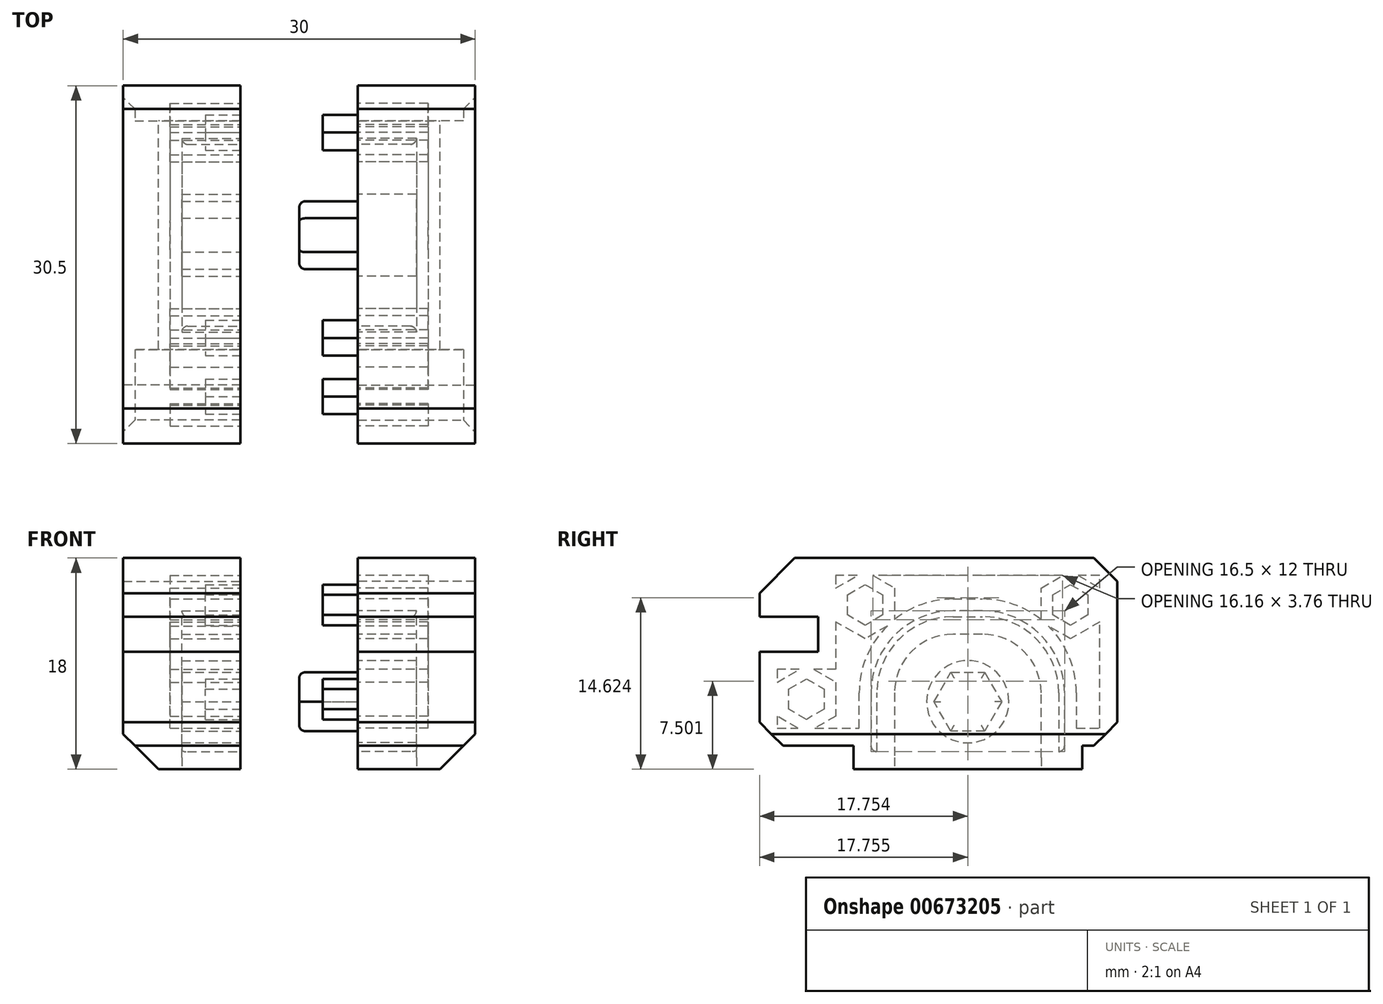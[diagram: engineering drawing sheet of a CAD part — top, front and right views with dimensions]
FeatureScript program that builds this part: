
annotation { "Feature Type Name" : "Feature", "Feature Type Description" : "" }
export const myFeature = defineFeature(function(context is Context, id is Id, definition is map)
    precondition{}
    {
        {
            var Q0;
            Q0=qCreatedBy(makeId("Right.planeOp"),FACE);
            var sketch = newSketch(context, id + "F0", { "sketchPlane" : qUnion([Q0])});
            skArc(sketch, "E0.0", {"start": v(4.44, 6.1) * mm, "mid": v(2.98, 9.63) * mm, "end": v(-0.56, 11.1) * mm});
            skLineSegment(sketch, "E0.1", {"start": v(4.44, 0.6) * mm, "end": v(4.44, 6.1) * mm});
            skLineSegment(sketch, "E0.2", {"start": v(-0.56, 11.1) * mm, "end": v(-3.06, 11.1) * mm});
            skArc(sketch, "E0.5", {"start": v(-3.06, 11.1) * mm, "mid": v(-6.6, 9.63) * mm, "end": v(-8.06, 6.1) * mm});
            skLineSegment(sketch, "E0.6", {"start": v(-8.06, 6.1) * mm, "end": v(-8.06, 0.6) * mm});
            skLineSegment(sketch, "E1", {"start": v(-1.8, 11.1) * mm, "end": v(-1.8, 5.34) * mm, "construction": true});
            skCircle(sketch, "E2", {"center": v(-1.8, 5.34) * mm, "radius": 3.5 * mm});
            skLineSegment(sketch, "E3.0", {"start": v(-10.06, 6.1) * mm, "end": v(-10.06, 1.6) * mm});
            skLineSegment(sketch, "E3.1", {"start": v(6.44, 1.6) * mm, "end": v(6.44, 6.1) * mm});
            skArc(sketch, "E3.2", {"start": v(6.44, 6.1) * mm, "mid": v(4.4, 11.04) * mm, "end": v(-0.56, 13.1) * mm});
            skLineSegment(sketch, "E3.3", {"start": v(-0.56, 13.1) * mm, "end": v(-3.06, 13.1) * mm});
            skArc(sketch, "E3.4", {"start": v(-3.06, 13.1) * mm, "mid": v(-8, 11.04) * mm, "end": v(-10.06, 6.1) * mm});
            skLineSegment(sketch, "E4", {"start": v(4.44, -0.4) * mm, "end": v(-8.06, -0.4) * mm});
            skPoint(sketch, "E5.visualSharp", {"position": v(6.44, -0.4) * mm});
            skArc(sketch, "E5.filletArc", {"start": v(4.44, -0.4) * mm, "mid": v(5.86, 0.18) * mm, "end": v(6.44, 1.6) * mm});
            skPoint(sketch, "E6.visualSharp", {"position": v(-10.06, -0.4) * mm});
            skArc(sketch, "E6.filletArc", {"start": v(-10.06, 1.6) * mm, "mid": v(-9.47, 0.18) * mm, "end": v(-8.06, -0.4) * mm});
            skLineSegment(sketch, "E7", {"start": v(-6.63, -0.4) * mm, "end": v(-6.63, 0.6) * mm, "construction": true});
            skLineSegment(sketch, "E8", {"start": v(-8.06, 0.6) * mm, "end": v(-8.06, -0.4) * mm});
            skLineSegment(sketch, "E9", {"start": v(4.44, 0.6) * mm, "end": v(4.44, -0.4) * mm});
            skSolve(sketch);
        }
        {
            var Q0;
            Q0=makeQuery(id+"F0.imprint","IMPRINT",FACE,{"disambiguationData":[TD([[makeQuery(id+"F0.imprint","IMPRINT",EDGE,{"derivedFrom":sQuery(id+"F0.wireOp",EDGE,"E0.0")}),1.0]])]});
            var Q1;
            Q1=makeQuery(id+"F0.imprint","IMPRINT",FACE,{"disambiguationData":[TD([[makeQuery(id+"F0.imprint","IMPRINT",EDGE,{"derivedFrom":sQuery(id+"F0.wireOp",EDGE,"E0.0")}),-1.0]])]});
            var Q2;
            Q2=makeQuery(id+"F0.imprint","IMPRINT",FACE,{"disambiguationData":[TD([[makeQuery(id+"F0.imprint","IMPRINT",EDGE,{"derivedFrom":sQuery(id+"F0.wireOp",EDGE,"E2")}),1.0]])]});
            extrude(context, id + "F1", {"entities" : qUnion([Q0, Q1, Q2]), "oppositeDirection" : true, "depth" : 10 * mm});
        }
        {
            var Q0;
            Q0=makeQuery(id+"F0.imprint","IMPRINT",FACE,{"disambiguationData":[TD([[makeQuery(id+"F0.imprint","IMPRINT",EDGE,{"derivedFrom":sQuery(id+"F0.wireOp",EDGE,"E0.0")}),1.0]])]});
            extrude(context, id + "F2", {"entities" : qUnion([Q0]), "operationType" : NewBodyOperationType.REMOVE, "oppositeDirection" : true, "depth" : 5 * mm});
        }
        {
            var Q0;
            {var subQ0=sQuery(id+"F0.wireOp",EDGE,"E6.filletArc");var subQ1=sQuery(id+"F0.wireOp",EDGE,"E5.filletArc");var subQ2=sQuery(id+"F0.wireOp",EDGE,"E3.4");var subQ3=sQuery(id+"F0.wireOp",EDGE,"E3.0");var subQ4=sQuery(id+"F0.wireOp",EDGE,"E3.1");var subQ5=sQuery(id+"F0.wireOp",EDGE,"E3.2");var subQ6=sQuery(id+"F0.wireOp",EDGE,"E3.3");Q0=makeQuery(id+"F2.boolean.opBoolean","SPLIT",FACE,{"disambiguationData":[TD([makeQuery(id+"F1.opExtrude","SWEPT_FACE",FACE,{"disambiguationData":[OSD([subQ3])]})])],"derivedFrom":makeQuery(id+"F1.opExtrude","CAP_FACE",FACE,{"disambiguationData":[OSD([subQ3,subQ4,subQ5,subQ6,subQ2,sQuery(id+"F0.wireOp",EDGE,"E4"),subQ1,subQ0])],"isStart":true})});}
            var sketch = newSketch(context, id + "F3", { "sketchPlane" : qUnion([Q0])});
            skArc(sketch, "E10.3", {"start": v(7.94, 6.1) * mm, "mid": v(5.45, 12.1) * mm, "end": v(-0.56, 14.6) * mm});
            skLineSegment(sketch, "E10.4", {"start": v(7.94, 1.6) * mm, "end": v(7.94, 6.1) * mm});
            skLineSegment(sketch, "E10.7", {"start": v(-0.56, 14.6) * mm, "end": v(-1.8, 14.6) * mm});
            skLineSegment(sketch, "E11", {"start": v(7.94, 1.6) * mm, "end": v(7.94, 1.6) * mm});
            skLineSegment(sketch, "E12", {"start": v(5.94, -0.4) * mm, "end": v(4.44, -0.4) * mm});
            skLineSegment(sketch, "E13", {"start": v(-1.8, 14.6) * mm, "end": v(-1.8, -1.79) * mm, "construction": true});
            skLineSegment(sketch, "E14.MirrorCS", {"start": v(-9.56, -0.4) * mm, "end": v(-8.06, -0.4) * mm});
            skArc(sketch, "E15.MirrorCS", {"start": v(-11.56, 6.1) * mm, "mid": v(-9.07, 12.1) * mm, "end": v(-3.06, 14.6) * mm});
            skLineSegment(sketch, "E16.MirrorCS", {"start": v(-11.56, 1.6) * mm, "end": v(-11.56, 1.6) * mm});
            skLineSegment(sketch, "E17.MirrorCS", {"start": v(-11.56, 1.6) * mm, "end": v(-11.56, 6.1) * mm});
            skLineSegment(sketch, "E18.MirrorCS", {"start": v(-3.06, 14.6) * mm, "end": v(-1.8, 14.6) * mm});
            skPoint(sketch, "E19.visualSharp", {"position": v(-11.56, -0.4) * mm});
            skArc(sketch, "E19.filletArc", {"start": v(-11.56, 1.6) * mm, "mid": v(-10.97, 0.18) * mm, "end": v(-9.56, -0.4) * mm});
            skPoint(sketch, "E20.visualSharp", {"position": v(7.94, -0.4) * mm});
            skArc(sketch, "E20.filletArc", {"start": v(5.94, -0.4) * mm, "mid": v(7.36, 0.18) * mm, "end": v(7.94, 1.6) * mm});
            skSolve(sketch);
        }
        {
            var Q0;
            Q0=qSketchRegion(id+"F3",true);
            var Q1;
            Q1=makeQuery(id+"F3.imprint","IMPRINT",FACE,{"disambiguationData":[TD([[makeQuery(id+"F3.imprint","IMPRINT",EDGE,{"derivedFrom":sQuery(id+"F3.wireOp",EDGE,"E10.3")}),1.0]])]});
            extrude(context, id + "F4", {"entities" : qUnion([Q0, Q1]), "operationType" : NewBodyOperationType.ADD, "oppositeDirection" : true, "depth" : 10 * mm});
        }
        {
            var Q0;
            {var subQ0=sQuery(id+"F0.wireOp",EDGE,"E6.filletArc");var subQ1=sQuery(id+"F0.wireOp",EDGE,"E5.filletArc");var subQ2=sQuery(id+"F0.wireOp",EDGE,"E3.4");var subQ3=sQuery(id+"F0.wireOp",EDGE,"E3.3");var subQ4=sQuery(id+"F0.wireOp",EDGE,"E3.2");var subQ5=sQuery(id+"F0.wireOp",EDGE,"E3.1");var subQ6=sQuery(id+"F0.wireOp",EDGE,"E3.0");Q0=makeQuery(id+"F4.boolean.opBoolean","MERGE",FACE,{"derivedFrom":[makeQuery(id+"F2.boolean.opBoolean","SPLIT",FACE,{"disambiguationData":[TD([makeQuery(id+"F1.opExtrude","SWEPT_FACE",FACE,{"disambiguationData":[OSD([subQ6])]})])],"derivedFrom":makeQuery(id+"F1.opExtrude","CAP_FACE",FACE,{"disambiguationData":[OSD([subQ6,subQ5,subQ4,subQ3,subQ2,sQuery(id+"F0.wireOp",EDGE,"E4"),subQ1,subQ0])],"isStart":true})}),makeQuery(id+"F4.opExtrude","CAP_FACE",FACE,{"disambiguationData":[OSD([subQ6,subQ5,subQ4,subQ3,subQ2,subQ1,subQ0,sQuery(id+"F3.wireOp",EDGE,"E10.3"),sQuery(id+"F3.wireOp",EDGE,"E10.4"),sQuery(id+"F3.wireOp",EDGE,"E10.7"),sQuery(id+"F3.wireOp",EDGE,"E12"),sQuery(id+"F3.wireOp",EDGE,"E14.MirrorCS"),sQuery(id+"F3.wireOp",EDGE,"E15.MirrorCS"),sQuery(id+"F3.wireOp",EDGE,"E17.MirrorCS"),sQuery(id+"F3.wireOp",EDGE,"E18.MirrorCS"),sQuery(id+"F3.wireOp",EDGE,"E19.filletArc"),sQuery(id+"F3.wireOp",EDGE,"E20.filletArc")])],"isStart":true})]});}
            var sketch = newSketch(context, id + "F5", { "sketchPlane" : qUnion([Q0])});
            skArc(sketch, "E21.0", {"start": v(-0.56, 12.6) * mm, "mid": v(4.04, 10.69) * mm, "end": v(5.94, 6.1) * mm});
            skLineSegment(sketch, "E21.1", {"start": v(-3.06, 12.6) * mm, "end": v(-0.56, 12.6) * mm});
            skArc(sketch, "E21.2", {"start": v(-9.56, 6.1) * mm, "mid": v(-7.65, 10.69) * mm, "end": v(-3.06, 12.6) * mm});
            skArc(sketch, "E21.3", {"start": v(6.44, 6.1) * mm, "mid": v(4.4, 11.04) * mm, "end": v(-0.56, 13.1) * mm});
            skLineSegment(sketch, "E21.4", {"start": v(6.44, 1.6) * mm, "end": v(6.44, 6.1) * mm});
            skArc(sketch, "E21.5", {"start": v(5.94, 1.1) * mm, "mid": v(6.3, 1.24) * mm, "end": v(6.44, 1.6) * mm});
            skLineSegment(sketch, "E21.6", {"start": v(5.94, 1.1) * mm, "end": v(5.94, 1.1) * mm});
            skLineSegment(sketch, "E21.7", {"start": v(-0.56, 13.1) * mm, "end": v(-3.06, 13.1) * mm});
            skArc(sketch, "E21.8", {"start": v(-3.06, 13.1) * mm, "mid": v(-8, 11.04) * mm, "end": v(-10.06, 6.1) * mm});
            skLineSegment(sketch, "E21.9", {"start": v(-10.06, 6.1) * mm, "end": v(-10.06, 1.6) * mm});
            skLineSegment(sketch, "E21.10", {"start": v(5.94, 6.1) * mm, "end": v(5.94, 1.1) * mm});
            skArc(sketch, "E21.11", {"start": v(-10.06, 1.6) * mm, "mid": v(-9.9, 1.24) * mm, "end": v(-9.56, 1.1) * mm});
            skLineSegment(sketch, "E21.12", {"start": v(-9.56, 1.1) * mm, "end": v(-9.56, 1.1) * mm});
            skLineSegment(sketch, "E21.13", {"start": v(-9.56, 1.1) * mm, "end": v(-9.56, 6.1) * mm});
            skLineSegment(sketch, "E22", {"start": v(-9.56, 1.1) * mm, "end": v(-9.56, -0.4) * mm});
            skLineSegment(sketch, "E23", {"start": v(5.94, 1.1) * mm, "end": v(5.94, -0.4) * mm});
            skSolve(sketch);
        }
        {
            var Q0;
            Q0=makeQuery(id+"F5.imprint","IMPRINT",FACE,{"disambiguationData":[TD([[makeQuery(id+"F5.imprint","IMPRINT",EDGE,{"derivedFrom":sQuery(id+"F5.wireOp",EDGE,"E21.0")}),-1.0]])]});
            extrude(context, id + "F6", {"entities" : qUnion([Q0]), "operationType" : NewBodyOperationType.REMOVE, "oppositeDirection" : true, "depth" : 5 * mm});
        }
        {
            var Q0;
            Q0=makeQuery(id+"F2.boolean.opBoolean","SPLIT",FACE,{"disambiguationData":[TD([makeQuery(id+"F2.opExtrude","SWEPT_FACE",FACE,{"disambiguationData":[OSD([sQuery(id+"F0.wireOp",EDGE,"E2")])]})])],"derivedFrom":makeQuery(id+"F1.opExtrude","CAP_FACE",FACE,{"disambiguationData":[OSD([sQuery(id+"F0.wireOp",EDGE,"E3.0"),sQuery(id+"F0.wireOp",EDGE,"E3.1"),sQuery(id+"F0.wireOp",EDGE,"E3.2"),sQuery(id+"F0.wireOp",EDGE,"E3.3"),sQuery(id+"F0.wireOp",EDGE,"E3.4"),sQuery(id+"F0.wireOp",EDGE,"E4"),sQuery(id+"F0.wireOp",EDGE,"E5.filletArc"),sQuery(id+"F0.wireOp",EDGE,"E6.filletArc")])],"isStart":true})});
            var sketch = newSketch(context, id + "F7", { "sketchPlane" : qUnion([Q0])});
            skLineSegment(sketch, "E24", {"start": v(-1.8, 5.34) * mm, "end": v(-1.8, 8.84) * mm, "construction": true});
            skCircle(sketch, "E25.cCircle", {"center": v(-1.8, 5.34) * mm, "radius": 2.5 * mm, "construction": true});
            skLineSegment(sketch, "E25.0", {"start": v(-0.36, 2.84) * mm, "end": v(-3.25, 2.84) * mm});
            skLineSegment(sketch, "E25.1", {"start": v(-3.25, 2.84) * mm, "end": v(-4.7, 5.34) * mm});
            skLineSegment(sketch, "E25.2", {"start": v(-4.7, 5.34) * mm, "end": v(-3.25, 7.84) * mm});
            skLineSegment(sketch, "E25.3", {"start": v(-3.25, 7.84) * mm, "end": v(-0.36, 7.84) * mm});
            skLineSegment(sketch, "E25.4", {"start": v(-0.36, 7.84) * mm, "end": v(1.08, 5.34) * mm});
            skLineSegment(sketch, "E25.5", {"start": v(1.08, 5.34) * mm, "end": v(-0.36, 2.84) * mm});
            skPoint(sketch, "E25.0.midPoint", {"position": v(-1.8, 2.84) * mm});
            skSolve(sketch);
        }
        {
            var Q0;
            Q0=qSketchRegion(id+"F7",true);
            extrude(context, id + "F8", {"entities" : qUnion([Q0]), "operationType" : NewBodyOperationType.REMOVE, "oppositeDirection" : true, "depth" : 5 * mm});
        }
        {
            var Q0;
            Q0=makeQuery(id+"F4.opExtrude","SWEPT_FACE",FACE,{"disambiguationData":[OSD([sQuery(id+"F3.wireOp",EDGE,"E17.MirrorCS")])]});
            extrude(context, id + "F9", {"entities" : qUnion([Q0]), "operationType" : NewBodyOperationType.ADD, "depth" : 3 * mm});
        }
        {
            var Q0;
            Q0=makeQuery(id+"F4.opExtrude","SWEPT_FACE",FACE,{"disambiguationData":[OSD([sQuery(id+"F3.wireOp",EDGE,"E10.4")])]});
            extrude(context, id + "F10", {"entities" : qUnion([Q0]), "operationType" : NewBodyOperationType.ADD, "depth" : 3 * mm});
        }
        {
            var Q0;
            Q0=makeQuery(id+"F4.opExtrude","SWEPT_FACE",FACE,{"disambiguationData":[OSD([sQuery(id+"F3.wireOp",EDGE,"E10.7"),sQuery(id+"F3.wireOp",EDGE,"E18.MirrorCS")])]});
            extrude(context, id + "F11", {"entities" : qUnion([Q0]), "operationType" : NewBodyOperationType.ADD, "depth" : 3 * mm});
        }
        {
            var Q0;
            {var subQ0=sQuery(id+"F3.wireOp",EDGE,"E18.MirrorCS");var subQ1=sQuery(id+"F3.wireOp",EDGE,"E10.7");var subQ2=sQuery(id+"F3.wireOp",EDGE,"E10.4");var subQ3=sQuery(id+"F3.wireOp",EDGE,"E17.MirrorCS");var subQ4=sQuery(id+"F0.wireOp",EDGE,"E6.filletArc");var subQ5=sQuery(id+"F0.wireOp",EDGE,"E5.filletArc");var subQ6=sQuery(id+"F0.wireOp",EDGE,"E3.4");var subQ7=sQuery(id+"F0.wireOp",EDGE,"E3.3");var subQ8=sQuery(id+"F0.wireOp",EDGE,"E3.2");var subQ9=sQuery(id+"F0.wireOp",EDGE,"E3.1");var subQ10=sQuery(id+"F0.wireOp",EDGE,"E3.0");Q0=makeQuery(id+"F11.boolean.opBoolean","MERGE",FACE,{"derivedFrom":[makeQuery(id+"F10.boolean.opBoolean","MERGE",FACE,{"derivedFrom":[makeQuery(id+"F9.boolean.opBoolean","MERGE",FACE,{"derivedFrom":[makeQuery(id+"F4.boolean.opBoolean","MERGE",FACE,{"derivedFrom":[makeQuery(id+"F1.opExtrude","CAP_FACE",FACE,{"disambiguationData":[OSD([subQ10,subQ9,subQ8,subQ7,subQ6,sQuery(id+"F0.wireOp",EDGE,"E4"),subQ5,subQ4])],"isStart":false}),makeQuery(id+"F4.opExtrude","CAP_FACE",FACE,{"disambiguationData":[OSD([subQ10,subQ9,subQ8,subQ7,subQ6,subQ5,subQ4,sQuery(id+"F3.wireOp",EDGE,"E10.3"),subQ2,subQ1,sQuery(id+"F3.wireOp",EDGE,"E12"),sQuery(id+"F3.wireOp",EDGE,"E14.MirrorCS"),sQuery(id+"F3.wireOp",EDGE,"E15.MirrorCS"),subQ3,subQ0,sQuery(id+"F3.wireOp",EDGE,"E19.filletArc"),sQuery(id+"F3.wireOp",EDGE,"E20.filletArc")])],"isStart":false})]}),makeQuery(id+"F9.opExtrude","SWEPT_FACE",FACE,{"disambiguationData":[OSD([subQ3]),TDD([makeQuery(id+"F4.opExtrude","CAP_EDGE",EDGE,{"disambiguationData":[OSD([subQ3])],"isStart":false})])]})]}),makeQuery(id+"F10.opExtrude","SWEPT_FACE",FACE,{"disambiguationData":[OSD([subQ2]),TDD([makeQuery(id+"F4.opExtrude","CAP_EDGE",EDGE,{"disambiguationData":[OSD([subQ2])],"isStart":false})])]})]}),makeQuery(id+"F11.opExtrude","SWEPT_FACE",FACE,{"disambiguationData":[OSD([subQ1,subQ0]),TDD([makeQuery(id+"F4.opExtrude","CAP_EDGE",EDGE,{"disambiguationData":[OSD([subQ1,subQ0])],"isStart":false})])]})]});}
            var sketch = newSketch(context, id + "F12", { "sketchPlane" : qUnion([Q0])});
            skLineSegment(sketch, "E26", {"start": v(0.56, 17.6) * mm, "end": v(-10.94, 17.6) * mm});
            skLineSegment(sketch, "E27", {"start": v(-10.94, 17.6) * mm, "end": v(-10.94, 6.1) * mm});
            skLineSegment(sketch, "E28", {"start": v(1.8, 17.6) * mm, "end": v(1.8, -0.4) * mm, "construction": true});
            skLineSegment(sketch, "E29.MirrorCS", {"start": v(3.06, 17.6) * mm, "end": v(14.56, 17.6) * mm});
            skLineSegment(sketch, "E30.MirrorCS", {"start": v(14.56, 17.6) * mm, "end": v(14.56, 6.1) * mm});
            skSolve(sketch);
        }
        {
            var Q0;
            Q0=qSketchRegion(id+"F12",true);
            var Q1;
            Q1=makeQuery(id+"F12.imprint","IMPRINT",FACE,{"disambiguationData":[TD([[makeQuery(id+"F12.imprint","IMPRINT",EDGE,{"derivedFrom":sQuery(id+"F12.wireOp",EDGE,"E26")}),1.0]])]});
            var Q2;
            Q2=makeQuery(id+"F12.imprint","IMPRINT",FACE,{"disambiguationData":[TD([[makeQuery(id+"F12.imprint","IMPRINT",EDGE,{"derivedFrom":sQuery(id+"F12.wireOp",EDGE,"E29.MirrorCS")}),-1.0]])]});
            extrude(context, id + "F13", {"entities" : qUnion([Q0, Q1, Q2]), "operationType" : NewBodyOperationType.ADD, "oppositeDirection" : true, "depth" : 10 * mm});
        }
        {
            var Q0;
            {var subQ0=sQuery(id+"F3.wireOp",EDGE,"E18.MirrorCS");var subQ1=sQuery(id+"F3.wireOp",EDGE,"E17.MirrorCS");var subQ2=sQuery(id+"F3.wireOp",EDGE,"E15.MirrorCS");var subQ3=sQuery(id+"F3.wireOp",EDGE,"E10.7");var subQ4=sQuery(id+"F3.wireOp",EDGE,"E10.4");var subQ5=sQuery(id+"F3.wireOp",EDGE,"E10.3");var subQ6=sQuery(id+"F0.wireOp",EDGE,"E6.filletArc");var subQ7=sQuery(id+"F0.wireOp",EDGE,"E5.filletArc");var subQ8=sQuery(id+"F0.wireOp",EDGE,"E3.4");var subQ9=sQuery(id+"F0.wireOp",EDGE,"E3.3");var subQ10=sQuery(id+"F0.wireOp",EDGE,"E3.2");var subQ11=sQuery(id+"F0.wireOp",EDGE,"E3.1");var subQ12=sQuery(id+"F0.wireOp",EDGE,"E3.0");Q0=makeQuery(id+"F13.boolean.opBoolean","MERGE",FACE,{"derivedFrom":[makeQuery(id+"F11.boolean.opBoolean","MERGE",FACE,{"derivedFrom":[makeQuery(id+"F10.boolean.opBoolean","MERGE",FACE,{"derivedFrom":[makeQuery(id+"F9.boolean.opBoolean","MERGE",FACE,{"derivedFrom":[makeQuery(id+"F4.boolean.opBoolean","MERGE",FACE,{"derivedFrom":[makeQuery(id+"F1.opExtrude","CAP_FACE",FACE,{"disambiguationData":[OSD([subQ12,subQ11,subQ10,subQ9,subQ8,sQuery(id+"F0.wireOp",EDGE,"E4"),subQ7,subQ6])],"isStart":false}),makeQuery(id+"F4.opExtrude","CAP_FACE",FACE,{"disambiguationData":[OSD([subQ12,subQ11,subQ10,subQ9,subQ8,subQ7,subQ6,subQ5,subQ4,subQ3,sQuery(id+"F3.wireOp",EDGE,"E12"),sQuery(id+"F3.wireOp",EDGE,"E14.MirrorCS"),subQ2,subQ1,subQ0,sQuery(id+"F3.wireOp",EDGE,"E19.filletArc"),sQuery(id+"F3.wireOp",EDGE,"E20.filletArc")])],"isStart":false})]}),makeQuery(id+"F9.opExtrude","SWEPT_FACE",FACE,{"disambiguationData":[OSD([subQ1]),TDD([makeQuery(id+"F4.opExtrude","CAP_EDGE",EDGE,{"disambiguationData":[OSD([subQ1])],"isStart":false})])]})]}),makeQuery(id+"F10.opExtrude","SWEPT_FACE",FACE,{"disambiguationData":[OSD([subQ4]),TDD([makeQuery(id+"F4.opExtrude","CAP_EDGE",EDGE,{"disambiguationData":[OSD([subQ4])],"isStart":false})])]})]}),makeQuery(id+"F11.opExtrude","SWEPT_FACE",FACE,{"disambiguationData":[OSD([subQ3,subQ0]),TDD([makeQuery(id+"F4.opExtrude","CAP_EDGE",EDGE,{"disambiguationData":[OSD([subQ3,subQ0])],"isStart":false})])]})]}),makeQuery(id+"F13.opExtrude","CAP_FACE",FACE,{"disambiguationData":[OSD([subQ5,subQ4,subQ3,sQuery(id+"F12.wireOp",EDGE,"E26"),sQuery(id+"F12.wireOp",EDGE,"E27")])],"isStart":true}),makeQuery(id+"F13.opExtrude","CAP_FACE",FACE,{"disambiguationData":[OSD([subQ2,subQ1,subQ0,sQuery(id+"F12.wireOp",EDGE,"E29.MirrorCS"),sQuery(id+"F12.wireOp",EDGE,"E30.MirrorCS")])],"isStart":true})]});}
            var sketch = newSketch(context, id + "F14", { "sketchPlane" : qUnion([Q0])});
            skPoint(sketch, "E31.oppositeSnap0", {"position": v(14.56, 9.6) * mm});
            skLineSegment(sketch, "E31.bottom", {"start": v(14.56, 1.6) * mm, "end": v(19.56, 1.6) * mm});
            skLineSegment(sketch, "E31.top", {"start": v(14.56, 9.6) * mm, "end": v(19.56, 9.6) * mm});
            skLineSegment(sketch, "E31.left", {"start": v(14.56, 1.6) * mm, "end": v(14.56, 9.6) * mm});
            skLineSegment(sketch, "E31.right", {"start": v(19.56, 1.6) * mm, "end": v(19.56, 9.6) * mm});
            skSolve(sketch);
        }
        {
            var Q0;
            Q0=qSketchRegion(id+"F14",true);
            extrude(context, id + "F15", {"entities" : qUnion([Q0]), "operationType" : NewBodyOperationType.ADD, "oppositeDirection" : true, "depth" : 10 * mm});
        }
        {
            var Q0;
            {var subQ0=sQuery(id+"F3.wireOp",EDGE,"E18.MirrorCS");var subQ1=sQuery(id+"F3.wireOp",EDGE,"E17.MirrorCS");var subQ2=sQuery(id+"F3.wireOp",EDGE,"E15.MirrorCS");var subQ3=sQuery(id+"F3.wireOp",EDGE,"E10.7");var subQ4=sQuery(id+"F3.wireOp",EDGE,"E10.4");var subQ5=sQuery(id+"F3.wireOp",EDGE,"E10.3");var subQ6=sQuery(id+"F0.wireOp",EDGE,"E6.filletArc");var subQ7=sQuery(id+"F0.wireOp",EDGE,"E5.filletArc");var subQ8=sQuery(id+"F0.wireOp",EDGE,"E3.4");var subQ9=sQuery(id+"F0.wireOp",EDGE,"E3.3");var subQ10=sQuery(id+"F0.wireOp",EDGE,"E3.2");var subQ11=sQuery(id+"F0.wireOp",EDGE,"E3.1");var subQ12=sQuery(id+"F0.wireOp",EDGE,"E3.0");Q0=makeQuery(id+"F15.boolean.opBoolean","MERGE",FACE,{"derivedFrom":[makeQuery(id+"F13.boolean.opBoolean","MERGE",FACE,{"derivedFrom":[makeQuery(id+"F11.boolean.opBoolean","MERGE",FACE,{"derivedFrom":[makeQuery(id+"F10.boolean.opBoolean","MERGE",FACE,{"derivedFrom":[makeQuery(id+"F9.boolean.opBoolean","MERGE",FACE,{"derivedFrom":[makeQuery(id+"F4.boolean.opBoolean","MERGE",FACE,{"derivedFrom":[makeQuery(id+"F2.boolean.opBoolean","SPLIT",FACE,{"disambiguationData":[TD([makeQuery(id+"F1.opExtrude","SWEPT_FACE",FACE,{"disambiguationData":[OSD([subQ12])]})])],"derivedFrom":makeQuery(id+"F1.opExtrude","CAP_FACE",FACE,{"disambiguationData":[OSD([subQ12,subQ11,subQ10,subQ9,subQ8,sQuery(id+"F0.wireOp",EDGE,"E4"),subQ7,subQ6])],"isStart":true})}),makeQuery(id+"F4.opExtrude","CAP_FACE",FACE,{"disambiguationData":[OSD([subQ12,subQ11,subQ10,subQ9,subQ8,subQ7,subQ6,subQ5,subQ4,subQ3,sQuery(id+"F3.wireOp",EDGE,"E12"),sQuery(id+"F3.wireOp",EDGE,"E14.MirrorCS"),subQ2,subQ1,subQ0,sQuery(id+"F3.wireOp",EDGE,"E19.filletArc"),sQuery(id+"F3.wireOp",EDGE,"E20.filletArc")])],"isStart":true})]}),makeQuery(id+"F9.opExtrude","SWEPT_FACE",FACE,{"disambiguationData":[OSD([subQ1]),TDD([makeQuery(id+"F4.opExtrude","CAP_EDGE",EDGE,{"disambiguationData":[OSD([subQ1])],"isStart":true})])]})]}),makeQuery(id+"F10.opExtrude","SWEPT_FACE",FACE,{"disambiguationData":[OSD([subQ4]),TDD([makeQuery(id+"F4.opExtrude","CAP_EDGE",EDGE,{"disambiguationData":[OSD([subQ4])],"isStart":true})])]})]}),makeQuery(id+"F11.opExtrude","SWEPT_FACE",FACE,{"disambiguationData":[OSD([subQ3,subQ0]),TDD([makeQuery(id+"F4.opExtrude","CAP_EDGE",EDGE,{"disambiguationData":[OSD([subQ3,subQ0])],"isStart":true})])]})]}),makeQuery(id+"F13.opExtrude","CAP_FACE",FACE,{"disambiguationData":[OSD([subQ5,subQ4,subQ3,sQuery(id+"F12.wireOp",EDGE,"E26"),sQuery(id+"F12.wireOp",EDGE,"E27")])],"isStart":false}),makeQuery(id+"F13.opExtrude","CAP_FACE",FACE,{"disambiguationData":[OSD([subQ2,subQ1,subQ0,sQuery(id+"F12.wireOp",EDGE,"E29.MirrorCS"),sQuery(id+"F12.wireOp",EDGE,"E30.MirrorCS")])],"isStart":false})]}),makeQuery(id+"F15.opExtrude","CAP_FACE",FACE,{"disambiguationData":[OSD([sQuery(id+"F14.wireOp",EDGE,"E31.bottom"),sQuery(id+"F14.wireOp",EDGE,"E31.top"),sQuery(id+"F14.wireOp",EDGE,"E31.left"),sQuery(id+"F14.wireOp",EDGE,"E31.right")])],"isStart":false})]});}
            var sketch = newSketch(context, id + "F16", { "sketchPlane" : qUnion([Q0])});
            skLineSegment(sketch, "E32.0", {"start": v(9.44, 3.1) * mm, "end": v(9.44, 16.1) * mm});
            skLineSegment(sketch, "E32.1", {"start": v(-18.06, 3.1) * mm, "end": v(-11.06, 3.1) * mm});
            skLineSegment(sketch, "E32.2", {"start": v(-18.06, 8.1) * mm, "end": v(-18.06, 3.1) * mm});
            skLineSegment(sketch, "E32.3", {"start": v(-13.06, 8.1) * mm, "end": v(-18.06, 8.1) * mm});
            skLineSegment(sketch, "E32.4", {"start": v(-13.06, 16.1) * mm, "end": v(-13.06, 8.1) * mm});
            skLineSegment(sketch, "E32.5", {"start": v(-11.06, 3.1) * mm, "end": v(-11.06, 6.1) * mm});
            skLineSegment(sketch, "E32.6", {"start": v(9.44, 16.1) * mm, "end": v(-13.06, 16.1) * mm});
            skArc(sketch, "E32.7", {"start": v(-11.06, 6.1) * mm, "mid": v(-8.71, 11.75) * mm, "end": v(-3.06, 14.1) * mm});
            skLineSegment(sketch, "E32.8", {"start": v(-3.06, 14.1) * mm, "end": v(-0.56, 14.1) * mm});
            skArc(sketch, "E32.9", {"start": v(-0.56, 14.1) * mm, "mid": v(5.1, 11.75) * mm, "end": v(7.44, 6.1) * mm});
            skLineSegment(sketch, "E32.10", {"start": v(7.44, 6.1) * mm, "end": v(7.44, 3.1) * mm});
            skLineSegment(sketch, "E32.11", {"start": v(7.44, 3.1) * mm, "end": v(9.44, 3.1) * mm});
            skCircle(sketch, "E33.cCircle", {"center": v(-15.56, 5.56) * mm, "radius": 2.5 * mm, "construction": true});
            skLineSegment(sketch, "E33.0", {"start": v(-18.06, 4.12) * mm, "end": v(-18.06, 7) * mm});
            skLineSegment(sketch, "E33.1", {"start": v(-18.06, 7) * mm, "end": v(-16.17, 8.1) * mm});
            skLineSegment(sketch, "E33.2", {"start": v(-14.94, 8.1) * mm, "end": v(-13.06, 7) * mm});
            skLineSegment(sketch, "E33.3", {"start": v(-13.06, 7) * mm, "end": v(-13.06, 4.12) * mm});
            skLineSegment(sketch, "E33.4", {"start": v(-13.06, 4.12) * mm, "end": v(-14.83, 3.1) * mm});
            skLineSegment(sketch, "E33.5", {"start": v(-16.28, 3.1) * mm, "end": v(-18.06, 4.12) * mm});
            skPoint(sketch, "E33.0.midPoint", {"position": v(-18.06, 5.56) * mm});
            skCircle(sketch, "E34.cCircle", {"center": v(-15.56, 5.56) * mm, "radius": 1.5 * mm, "construction": true});
            skLineSegment(sketch, "E34.0", {"start": v(-17.06, 4.7) * mm, "end": v(-17.06, 6.43) * mm});
            skLineSegment(sketch, "E34.1", {"start": v(-17.06, 6.43) * mm, "end": v(-15.56, 7.3) * mm});
            skLineSegment(sketch, "E34.2", {"start": v(-15.56, 7.3) * mm, "end": v(-14.06, 6.43) * mm});
            skLineSegment(sketch, "E34.3", {"start": v(-14.06, 6.43) * mm, "end": v(-14.06, 4.7) * mm});
            skLineSegment(sketch, "E34.4", {"start": v(-14.06, 4.7) * mm, "end": v(-15.56, 3.83) * mm});
            skLineSegment(sketch, "E34.5", {"start": v(-15.56, 3.83) * mm, "end": v(-17.06, 4.7) * mm});
            skPoint(sketch, "E34.0.midPoint", {"position": v(-17.06, 5.56) * mm});
            skPoint(sketch, "E35.orphan", {"position": v(-15.56, 2.67) * mm});
            skPoint(sketch, "E36.orphan", {"position": v(-15.56, 8.45) * mm});
            skCircle(sketch, "E37.cCircle", {"center": v(-10.56, 13.6) * mm, "radius": 2.5 * mm, "construction": true});
            skLineSegment(sketch, "E37.0", {"start": v(-13.06, 12.15) * mm, "end": v(-13.06, 15.03) * mm});
            skLineSegment(sketch, "E37.1", {"start": v(-13.06, 15.03) * mm, "end": v(-11.23, 16.1) * mm});
            skLineSegment(sketch, "E37.2", {"start": v(-9.89, 16.1) * mm, "end": v(-8.06, 15.03) * mm});
            skLineSegment(sketch, "E37.3", {"start": v(-8.06, 15.03) * mm, "end": v(-8.06, 12.34) * mm});
            skLineSegment(sketch, "E37.4", {"start": v(-8.66, 11.8) * mm, "end": v(-10.56, 10.7) * mm});
            skLineSegment(sketch, "E37.5", {"start": v(-10.56, 10.7) * mm, "end": v(-13.06, 12.15) * mm});
            skPoint(sketch, "E37.0.midPoint", {"position": v(-13.06, 13.6) * mm});
            skCircle(sketch, "E38.cCircle", {"center": v(-10.56, 13.6) * mm, "radius": 1.5 * mm, "construction": true});
            skLineSegment(sketch, "E38.0", {"start": v(-12.06, 12.73) * mm, "end": v(-12.06, 14.46) * mm});
            skLineSegment(sketch, "E38.1", {"start": v(-12.06, 14.46) * mm, "end": v(-10.56, 15.32) * mm});
            skLineSegment(sketch, "E38.2", {"start": v(-10.56, 15.32) * mm, "end": v(-9.06, 14.46) * mm});
            skLineSegment(sketch, "E38.3", {"start": v(-9.06, 14.46) * mm, "end": v(-9.06, 12.73) * mm});
            skLineSegment(sketch, "E38.4", {"start": v(-9.06, 12.73) * mm, "end": v(-10.56, 11.86) * mm});
            skLineSegment(sketch, "E38.5", {"start": v(-10.56, 11.86) * mm, "end": v(-12.06, 12.73) * mm});
            skPoint(sketch, "E38.0.midPoint", {"position": v(-12.06, 13.6) * mm});
            skPoint(sketch, "E39.orphan", {"position": v(-8.06, 12.15) * mm});
            skPoint(sketch, "E40.orphan", {"position": v(-10.56, 16.48) * mm});
            skCircle(sketch, "E41.cCircle", {"center": v(6.94, 13.6) * mm, "radius": 2.5 * mm, "construction": true});
            skLineSegment(sketch, "E41.0", {"start": v(9.44, 15.03) * mm, "end": v(9.44, 12.15) * mm});
            skLineSegment(sketch, "E41.1", {"start": v(9.44, 12.15) * mm, "end": v(6.94, 10.7) * mm});
            skLineSegment(sketch, "E41.2", {"start": v(6.94, 10.7) * mm, "end": v(5.05, 11.8) * mm});
            skLineSegment(sketch, "E41.3", {"start": v(4.44, 12.34) * mm, "end": v(4.44, 15.03) * mm});
            skLineSegment(sketch, "E41.4", {"start": v(4.44, 15.03) * mm, "end": v(6.27, 16.1) * mm});
            skLineSegment(sketch, "E41.5", {"start": v(7.61, 16.1) * mm, "end": v(9.44, 15.03) * mm});
            skPoint(sketch, "E41.0.midPoint", {"position": v(9.44, 13.6) * mm});
            skCircle(sketch, "E42.cCircle", {"center": v(6.94, 13.6) * mm, "radius": 1.5 * mm, "construction": true});
            skLineSegment(sketch, "E42.0", {"start": v(5.44, 12.73) * mm, "end": v(5.44, 14.46) * mm});
            skLineSegment(sketch, "E42.1", {"start": v(5.44, 14.46) * mm, "end": v(6.94, 15.32) * mm});
            skLineSegment(sketch, "E42.2", {"start": v(6.94, 15.32) * mm, "end": v(8.44, 14.46) * mm});
            skLineSegment(sketch, "E42.3", {"start": v(8.44, 14.46) * mm, "end": v(8.44, 12.73) * mm});
            skLineSegment(sketch, "E42.4", {"start": v(8.44, 12.73) * mm, "end": v(6.94, 11.86) * mm});
            skLineSegment(sketch, "E42.5", {"start": v(6.94, 11.86) * mm, "end": v(5.44, 12.73) * mm});
            skPoint(sketch, "E42.0.midPoint", {"position": v(5.44, 13.6) * mm});
            skPoint(sketch, "E43.orphan", {"position": v(4.44, 12.15) * mm});
            skPoint(sketch, "E44.orphan", {"position": v(6.94, 16.48) * mm});
            skSolve(sketch);
        }
        {
            var Q0;
            Q0=makeQuery(id+"F16.imprint","IMPRINT",FACE,{"disambiguationData":[TD([[makeQuery(id+"F16.imprint","IMPRINT",EDGE,{"derivedFrom":sQuery(id+"F16.wireOp",EDGE,"E34.0")}),-1.0]])]});
            var Q1;
            {var subQ3=sQuery(id+"F16.wireOp",EDGE,"E33.1");Q1=makeQuery(id+"F16.imprint","IMPRINT",FACE,{"disambiguationData":[TD([[makeQuery(id+"F16.imprint","IMPRINT",EDGE,{"derivedFrom":subQ3}),1.0]])]});}
            var Q2;
            {var subQ3=sQuery(id+"F16.wireOp",EDGE,"E33.5");Q2=makeQuery(id+"F16.imprint","IMPRINT",FACE,{"disambiguationData":[TD([[makeQuery(id+"F16.imprint","IMPRINT",EDGE,{"derivedFrom":subQ3}),1.0]])]});}
            var Q3;
            {var subQ5=sQuery(id+"F16.wireOp",EDGE,"E32.5");Q3=makeQuery(id+"F16.imprint","IMPRINT",FACE,{"disambiguationData":[TD([[makeQuery(id+"F16.imprint","IMPRINT",EDGE,{"derivedFrom":subQ5}),1.0]])]});}
            var Q4;
            Q4=makeQuery(id+"F16.imprint","IMPRINT",FACE,{"disambiguationData":[TD([[makeQuery(id+"F16.imprint","IMPRINT",EDGE,{"derivedFrom":sQuery(id+"F16.wireOp",EDGE,"E38.0")}),-1.0]])]});
            var Q5;
            {var subQ3=sQuery(id+"F16.wireOp",EDGE,"E37.1");Q5=makeQuery(id+"F16.imprint","IMPRINT",FACE,{"disambiguationData":[TD([[makeQuery(id+"F16.imprint","IMPRINT",EDGE,{"derivedFrom":subQ3}),1.0]])]});}
            var Q6;
            {var subQ1=sQuery(id+"F16.wireOp",EDGE,"E32.8");Q6=makeQuery(id+"F16.imprint","IMPRINT",FACE,{"disambiguationData":[TD([[makeQuery(id+"F16.imprint","IMPRINT",EDGE,{"derivedFrom":subQ1}),1.0]])]});}
            var Q7;
            {var subQ2=sQuery(id+"F16.wireOp",EDGE,"E32.10");Q7=makeQuery(id+"F16.imprint","IMPRINT",FACE,{"disambiguationData":[TD([[makeQuery(id+"F16.imprint","IMPRINT",EDGE,{"derivedFrom":subQ2}),1.0]])]});}
            var Q8;
            {var subQ3=sQuery(id+"F16.wireOp",EDGE,"E41.5");Q8=makeQuery(id+"F16.imprint","IMPRINT",FACE,{"disambiguationData":[TD([[makeQuery(id+"F16.imprint","IMPRINT",EDGE,{"derivedFrom":subQ3}),1.0]])]});}
            var Q9;
            Q9=makeQuery(id+"F16.imprint","IMPRINT",FACE,{"disambiguationData":[TD([[makeQuery(id+"F16.imprint","IMPRINT",EDGE,{"derivedFrom":sQuery(id+"F16.wireOp",EDGE,"E42.0")}),-1.0]])]});
            extrude(context, id + "F17", {"entities" : qUnion([Q0, Q1, Q2, Q3, Q4, Q5, Q6, Q7, Q8, Q9]), "operationType" : NewBodyOperationType.REMOVE, "oppositeDirection" : true, "depth" : 3 * mm});
        }
        {
            var Q0;
            Q0=makeQuery(id+"F17.boolean.opBoolean","COPY",FACE,{"derivedFrom":makeQuery(id+"F17.opExtrude","CAP_FACE",FACE,{"disambiguationData":[OSD([sQuery(id+"F16.wireOp",EDGE,"E32.1"),sQuery(id+"F16.wireOp",EDGE,"E32.3"),sQuery(id+"F16.wireOp",EDGE,"E32.4"),sQuery(id+"F16.wireOp",EDGE,"E32.5"),sQuery(id+"F16.wireOp",EDGE,"E32.7"),sQuery(id+"F16.wireOp",EDGE,"E33.2"),sQuery(id+"F16.wireOp",EDGE,"E33.3"),sQuery(id+"F16.wireOp",EDGE,"E33.4"),sQuery(id+"F16.wireOp",EDGE,"E37.4"),sQuery(id+"F16.wireOp",EDGE,"E37.5")])],"isStart":false})});
            var Q1;
            Q1=makeQuery(id+"F17.boolean.opBoolean","COPY",FACE,{"derivedFrom":makeQuery(id+"F17.opExtrude","CAP_FACE",FACE,{"disambiguationData":[OSD([sQuery(id+"F16.wireOp",EDGE,"E32.6"),sQuery(id+"F16.wireOp",EDGE,"E32.7"),sQuery(id+"F16.wireOp",EDGE,"E32.8"),sQuery(id+"F16.wireOp",EDGE,"E32.9"),sQuery(id+"F16.wireOp",EDGE,"E37.2"),sQuery(id+"F16.wireOp",EDGE,"E37.3"),sQuery(id+"F16.wireOp",EDGE,"E41.3"),sQuery(id+"F16.wireOp",EDGE,"E41.4")])],"isStart":false})});
            var Q2;
            Q2=makeQuery(id+"F17.boolean.opBoolean","COPY",FACE,{"derivedFrom":makeQuery(id+"F17.opExtrude","CAP_FACE",FACE,{"disambiguationData":[OSD([sQuery(id+"F16.wireOp",EDGE,"E32.4"),sQuery(id+"F16.wireOp",EDGE,"E32.6"),sQuery(id+"F16.wireOp",EDGE,"E37.1")])],"isStart":false})});
            var Q3;
            Q3=makeQuery(id+"F17.boolean.opBoolean","COPY",FACE,{"derivedFrom":makeQuery(id+"F17.opExtrude","CAP_FACE",FACE,{"disambiguationData":[OSD([sQuery(id+"F16.wireOp",EDGE,"E32.1"),sQuery(id+"F16.wireOp",EDGE,"E32.2"),sQuery(id+"F16.wireOp",EDGE,"E33.5")])],"isStart":false})});
            var Q4;
            Q4=makeQuery(id+"F17.boolean.opBoolean","COPY",FACE,{"derivedFrom":makeQuery(id+"F17.opExtrude","CAP_FACE",FACE,{"disambiguationData":[OSD([sQuery(id+"F16.wireOp",EDGE,"E32.2"),sQuery(id+"F16.wireOp",EDGE,"E32.3"),sQuery(id+"F16.wireOp",EDGE,"E33.1")])],"isStart":false})});
            var Q5;
            Q5=makeQuery(id+"F17.boolean.opBoolean","COPY",FACE,{"derivedFrom":makeQuery(id+"F17.opExtrude","CAP_FACE",FACE,{"disambiguationData":[OSD([sQuery(id+"F16.wireOp",EDGE,"E32.0"),sQuery(id+"F16.wireOp",EDGE,"E32.9"),sQuery(id+"F16.wireOp",EDGE,"E32.10"),sQuery(id+"F16.wireOp",EDGE,"E32.11"),sQuery(id+"F16.wireOp",EDGE,"E41.1"),sQuery(id+"F16.wireOp",EDGE,"E41.2")])],"isStart":false})});
            var Q6;
            Q6=makeQuery(id+"F17.boolean.opBoolean","COPY",FACE,{"derivedFrom":makeQuery(id+"F17.opExtrude","CAP_FACE",FACE,{"disambiguationData":[OSD([sQuery(id+"F16.wireOp",EDGE,"E32.0"),sQuery(id+"F16.wireOp",EDGE,"E32.6"),sQuery(id+"F16.wireOp",EDGE,"E41.5")])],"isStart":false})});
            extrude(context, id + "F18", {"entities" : qUnion([Q0, Q1, Q2, Q3, Q4, Q5, Q6]), "operationType" : NewBodyOperationType.REMOVE, "oppositeDirection" : true, "depth" : 3 * mm});
        }
        {
            var Q0;
            Q0=makeQuery(id+"F13.opExtrude","SWEPT_EDGE",EDGE,{"disambiguationData":[OSD([sQuery(id+"F12.wireOp",EDGE,"E26"),sQuery(id+"F12.wireOp",EDGE,"E27")])]});
            var Q1;
            Q1=makeQuery(id+"F10.opExtrude","CAP_EDGE",EDGE,{"disambiguationData":[OSD([sQuery(id+"F3.wireOp",EDGE,"E10.4"),sQuery(id+"F3.wireOp",EDGE,"E20.filletArc")])],"isStart":false});
            var Q2;
            Q2=makeQuery(id+"F15.opExtrude","SWEPT_EDGE",EDGE,{"disambiguationData":[OSD([sQuery(id+"F14.wireOp",EDGE,"E31.bottom"),sQuery(id+"F14.wireOp",EDGE,"E31.right")])]});
            chamfer(context, id + "F19", {"entities" : qUnion([Q0, Q1, Q2]), "width" : 2 * mm, "tangentPropagation" : true});
        }
        {
            var Q0;
            {var subQ0=sQuery(id+"F3.wireOp",EDGE,"E18.MirrorCS");var subQ1=sQuery(id+"F3.wireOp",EDGE,"E17.MirrorCS");var subQ2=sQuery(id+"F3.wireOp",EDGE,"E15.MirrorCS");var subQ3=sQuery(id+"F3.wireOp",EDGE,"E10.7");var subQ4=sQuery(id+"F3.wireOp",EDGE,"E10.4");var subQ5=sQuery(id+"F3.wireOp",EDGE,"E10.3");var subQ6=sQuery(id+"F0.wireOp",EDGE,"E6.filletArc");var subQ7=sQuery(id+"F0.wireOp",EDGE,"E5.filletArc");var subQ8=sQuery(id+"F0.wireOp",EDGE,"E3.4");var subQ9=sQuery(id+"F0.wireOp",EDGE,"E3.3");var subQ10=sQuery(id+"F0.wireOp",EDGE,"E3.2");var subQ11=sQuery(id+"F0.wireOp",EDGE,"E3.1");var subQ12=sQuery(id+"F0.wireOp",EDGE,"E3.0");Q0=makeQuery(id+"F15.boolean.opBoolean","MERGE",FACE,{"derivedFrom":[makeQuery(id+"F13.boolean.opBoolean","MERGE",FACE,{"derivedFrom":[makeQuery(id+"F11.boolean.opBoolean","MERGE",FACE,{"derivedFrom":[makeQuery(id+"F10.boolean.opBoolean","MERGE",FACE,{"derivedFrom":[makeQuery(id+"F9.boolean.opBoolean","MERGE",FACE,{"derivedFrom":[makeQuery(id+"F4.boolean.opBoolean","MERGE",FACE,{"derivedFrom":[makeQuery(id+"F1.opExtrude","CAP_FACE",FACE,{"disambiguationData":[OSD([subQ12,subQ11,subQ10,subQ9,subQ8,sQuery(id+"F0.wireOp",EDGE,"E4"),subQ7,subQ6])],"isStart":false}),makeQuery(id+"F4.opExtrude","CAP_FACE",FACE,{"disambiguationData":[OSD([subQ12,subQ11,subQ10,subQ9,subQ8,subQ7,subQ6,subQ5,subQ4,subQ3,sQuery(id+"F3.wireOp",EDGE,"E12"),sQuery(id+"F3.wireOp",EDGE,"E14.MirrorCS"),subQ2,subQ1,subQ0,sQuery(id+"F3.wireOp",EDGE,"E19.filletArc"),sQuery(id+"F3.wireOp",EDGE,"E20.filletArc")])],"isStart":false})]}),makeQuery(id+"F9.opExtrude","SWEPT_FACE",FACE,{"disambiguationData":[OSD([subQ1]),TDD([makeQuery(id+"F4.opExtrude","CAP_EDGE",EDGE,{"disambiguationData":[OSD([subQ1])],"isStart":false})])]})]}),makeQuery(id+"F10.opExtrude","SWEPT_FACE",FACE,{"disambiguationData":[OSD([subQ4]),TDD([makeQuery(id+"F4.opExtrude","CAP_EDGE",EDGE,{"disambiguationData":[OSD([subQ4])],"isStart":false})])]})]}),makeQuery(id+"F11.opExtrude","SWEPT_FACE",FACE,{"disambiguationData":[OSD([subQ3,subQ0]),TDD([makeQuery(id+"F4.opExtrude","CAP_EDGE",EDGE,{"disambiguationData":[OSD([subQ3,subQ0])],"isStart":false})])]})]}),makeQuery(id+"F13.opExtrude","CAP_FACE",FACE,{"disambiguationData":[OSD([subQ5,subQ4,subQ3,sQuery(id+"F12.wireOp",EDGE,"E26"),sQuery(id+"F12.wireOp",EDGE,"E27")])],"isStart":true}),makeQuery(id+"F13.opExtrude","CAP_FACE",FACE,{"disambiguationData":[OSD([subQ2,subQ1,subQ0,sQuery(id+"F12.wireOp",EDGE,"E29.MirrorCS"),sQuery(id+"F12.wireOp",EDGE,"E30.MirrorCS")])],"isStart":true})]}),makeQuery(id+"F15.opExtrude","CAP_FACE",FACE,{"disambiguationData":[OSD([sQuery(id+"F14.wireOp",EDGE,"E31.bottom"),sQuery(id+"F14.wireOp",EDGE,"E31.top"),sQuery(id+"F14.wireOp",EDGE,"E31.left"),sQuery(id+"F14.wireOp",EDGE,"E31.right")])],"isStart":true})]});}
            var sketch = newSketch(context, id + "F20", { "sketchPlane" : qUnion([Q0])});
            skLineSegment(sketch, "E45", {"start": v(11.56, 1.6) * mm, "end": v(11.56, -0.4) * mm});
            skLineSegment(sketch, "E46", {"start": v(11.56, -0.4) * mm, "end": v(9.56, -0.4) * mm});
            skLineSegment(sketch, "E47", {"start": v(1.8, -0.4) * mm, "end": v(1.8, 1.28) * mm, "construction": true});
            skLineSegment(sketch, "E48.MirrorCS", {"start": v(-7.94, -0.4) * mm, "end": v(-5.94, -0.4) * mm});
            skLineSegment(sketch, "E49.MirrorCS", {"start": v(-7.94, 1.6) * mm, "end": v(-7.94, -0.4) * mm});
            skSolve(sketch);
        }
        {
            var Q0;
            Q0=makeQuery(id+"F20.imprint","IMPRINT",FACE,{"disambiguationData":[TD([[makeQuery(id+"F20.imprint","IMPRINT",EDGE,{"derivedFrom":sQuery(id+"F20.wireOp",EDGE,"E48.MirrorCS")}),1.0]])]});
            var Q1;
            Q1=makeQuery(id+"F20.imprint","IMPRINT",FACE,{"disambiguationData":[TD([[makeQuery(id+"F20.imprint","IMPRINT",EDGE,{"derivedFrom":sQuery(id+"F20.wireOp",EDGE,"E45")}),-1.0]])]});
            extrude(context, id + "F21", {"entities" : qUnion([Q0, Q1]), "operationType" : NewBodyOperationType.ADD, "oppositeDirection" : true, "depth" : 10 * mm});
        }
        {
            var Q0;
            Q0=makeQuery(id+"F2.boolean.opBoolean","COPY",EDGE,{"derivedFrom":makeQuery(id+"F2.opExtrude","CAP_EDGE",EDGE,{"disambiguationData":[OSD([sQuery(id+"F0.wireOp",EDGE,"E4")])],"isStart":false})});
            var Q1;
            {var subQ0=sQuery(id+"F3.wireOp",EDGE,"E20.filletArc");var subQ1=sQuery(id+"F3.wireOp",EDGE,"E12");Q1=makeQuery(id+"F21.boolean.opBoolean","MERGE",EDGE,{"derivedFrom":[makeQuery(id+"F6.boolean.opBoolean","MERGE",EDGE,{"derivedFrom":[makeQuery(id+"F4.opExtrude","SWEPT_EDGE",EDGE,{"disambiguationData":[OSD([subQ1,subQ0])]}),makeQuery(id+"F6.opExtrude","SWEPT_EDGE",EDGE,{"disambiguationData":[OSD([subQ1,subQ0,sQuery(id+"F5.wireOp",EDGE,"E23")])]})]}),makeQuery(id+"F21.opExtrude","SWEPT_EDGE",EDGE,{"disambiguationData":[OSD([subQ1,subQ0,sQuery(id+"F20.wireOp",EDGE,"E48.MirrorCS")])]})]});}
            var Q2;
            {var subQ0=sQuery(id+"F3.wireOp",EDGE,"E19.filletArc");var subQ1=sQuery(id+"F3.wireOp",EDGE,"E14.MirrorCS");Q2=makeQuery(id+"F21.boolean.opBoolean","MERGE",EDGE,{"derivedFrom":[makeQuery(id+"F6.boolean.opBoolean","MERGE",EDGE,{"derivedFrom":[makeQuery(id+"F4.opExtrude","SWEPT_EDGE",EDGE,{"disambiguationData":[OSD([subQ1,subQ0])]}),makeQuery(id+"F6.opExtrude","SWEPT_EDGE",EDGE,{"disambiguationData":[OSD([subQ1,subQ0,sQuery(id+"F5.wireOp",EDGE,"E22")])]})]}),makeQuery(id+"F21.opExtrude","SWEPT_EDGE",EDGE,{"disambiguationData":[OSD([subQ1,subQ0,sQuery(id+"F20.wireOp",EDGE,"E46")])]})]});}
            var Q3;
            Q3=makeQuery(id+"F6.boolean.opBoolean","COPY",EDGE,{"derivedFrom":makeQuery(id+"F6.opExtrude","CAP_EDGE",EDGE,{"disambiguationData":[OSD([sQuery(id+"F5.wireOp",EDGE,"E21.13"),sQuery(id+"F5.wireOp",EDGE,"E22")])],"isStart":false})});
            fillet(context, id + "F22", {"entities" : qUnion([Q0, Q1, Q2, Q3]), "radius" : .5 * mm, "tangentPropagation" : true, "allowEdgeOverflow" : false});
        }
        {
            var Q0;
            Q0=makeQuery(id+"F1.opExtrude","CAP_EDGE",EDGE,{"disambiguationData":[OSD([sQuery(id+"F0.wireOp",EDGE,"E4")])],"isStart":false});
            chamfer(context, id + "F23", {"entities" : qUnion([Q0]), "width" : 3 * mm, "tangentPropagation" : true});
        }
        {
            var Q0;
            {var subQ0=sQuery(id+"F3.wireOp",EDGE,"E20.filletArc");var subQ1=sQuery(id+"F3.wireOp",EDGE,"E19.filletArc");var subQ2=sQuery(id+"F3.wireOp",EDGE,"E18.MirrorCS");var subQ3=sQuery(id+"F3.wireOp",EDGE,"E17.MirrorCS");var subQ4=sQuery(id+"F3.wireOp",EDGE,"E15.MirrorCS");var subQ5=sQuery(id+"F3.wireOp",EDGE,"E10.7");var subQ6=sQuery(id+"F3.wireOp",EDGE,"E10.4");var subQ7=sQuery(id+"F3.wireOp",EDGE,"E10.3");var subQ8=sQuery(id+"F0.wireOp",EDGE,"E6.filletArc");var subQ9=sQuery(id+"F0.wireOp",EDGE,"E5.filletArc");var subQ10=sQuery(id+"F0.wireOp",EDGE,"E3.4");var subQ11=sQuery(id+"F0.wireOp",EDGE,"E3.3");var subQ12=sQuery(id+"F0.wireOp",EDGE,"E3.2");var subQ13=sQuery(id+"F0.wireOp",EDGE,"E3.1");var subQ14=sQuery(id+"F0.wireOp",EDGE,"E3.0");Q0=makeQuery(id+"F21.boolean.opBoolean","MERGE",FACE,{"derivedFrom":[makeQuery(id+"F15.boolean.opBoolean","MERGE",FACE,{"derivedFrom":[makeQuery(id+"F13.boolean.opBoolean","MERGE",FACE,{"derivedFrom":[makeQuery(id+"F11.boolean.opBoolean","MERGE",FACE,{"derivedFrom":[makeQuery(id+"F10.boolean.opBoolean","MERGE",FACE,{"derivedFrom":[makeQuery(id+"F9.boolean.opBoolean","MERGE",FACE,{"derivedFrom":[makeQuery(id+"F4.boolean.opBoolean","MERGE",FACE,{"derivedFrom":[makeQuery(id+"F1.opExtrude","CAP_FACE",FACE,{"disambiguationData":[OSD([subQ14,subQ13,subQ12,subQ11,subQ10,sQuery(id+"F0.wireOp",EDGE,"E4"),subQ9,subQ8])],"isStart":false}),makeQuery(id+"F4.opExtrude","CAP_FACE",FACE,{"disambiguationData":[OSD([subQ14,subQ13,subQ12,subQ11,subQ10,subQ9,subQ8,subQ7,subQ6,subQ5,sQuery(id+"F3.wireOp",EDGE,"E12"),sQuery(id+"F3.wireOp",EDGE,"E14.MirrorCS"),subQ4,subQ3,subQ2,subQ1,subQ0])],"isStart":false})]}),makeQuery(id+"F9.opExtrude","SWEPT_FACE",FACE,{"disambiguationData":[OSD([subQ3]),TDD([makeQuery(id+"F4.opExtrude","CAP_EDGE",EDGE,{"disambiguationData":[OSD([subQ3])],"isStart":false})])]})]}),makeQuery(id+"F10.opExtrude","SWEPT_FACE",FACE,{"disambiguationData":[OSD([subQ6]),TDD([makeQuery(id+"F4.opExtrude","CAP_EDGE",EDGE,{"disambiguationData":[OSD([subQ6])],"isStart":false})])]})]}),makeQuery(id+"F11.opExtrude","SWEPT_FACE",FACE,{"disambiguationData":[OSD([subQ5,subQ2]),TDD([makeQuery(id+"F4.opExtrude","CAP_EDGE",EDGE,{"disambiguationData":[OSD([subQ5,subQ2])],"isStart":false})])]})]}),makeQuery(id+"F13.opExtrude","CAP_FACE",FACE,{"disambiguationData":[OSD([subQ7,subQ6,subQ5,sQuery(id+"F12.wireOp",EDGE,"E26"),sQuery(id+"F12.wireOp",EDGE,"E27")])],"isStart":true}),makeQuery(id+"F13.opExtrude","CAP_FACE",FACE,{"disambiguationData":[OSD([subQ4,subQ3,subQ2,sQuery(id+"F12.wireOp",EDGE,"E29.MirrorCS"),sQuery(id+"F12.wireOp",EDGE,"E30.MirrorCS")])],"isStart":true})]}),makeQuery(id+"F15.opExtrude","CAP_FACE",FACE,{"disambiguationData":[OSD([sQuery(id+"F14.wireOp",EDGE,"E31.bottom"),sQuery(id+"F14.wireOp",EDGE,"E31.top"),sQuery(id+"F14.wireOp",EDGE,"E31.left"),sQuery(id+"F14.wireOp",EDGE,"E31.right")])],"isStart":true})]}),makeQuery(id+"F21.opExtrude","CAP_FACE",FACE,{"disambiguationData":[OSD([subQ1,sQuery(id+"F20.wireOp",EDGE,"E45"),sQuery(id+"F20.wireOp",EDGE,"E46")])],"isStart":true}),makeQuery(id+"F21.opExtrude","CAP_FACE",FACE,{"disambiguationData":[OSD([subQ0,sQuery(id+"F20.wireOp",EDGE,"E48.MirrorCS"),sQuery(id+"F20.wireOp",EDGE,"E49.MirrorCS")])],"isStart":true})]});}
            var sketch = newSketch(context, id + "F24", { "sketchPlane" : qUnion([Q0])});
            skLineSegment(sketch, "E50.bottom", {"start": v(14.56, 17.6) * mm, "end": v(19.56, 17.6) * mm});
            skLineSegment(sketch, "E50.top", {"start": v(14.56, 12.6) * mm, "end": v(19.56, 12.6) * mm});
            skLineSegment(sketch, "E50.left", {"start": v(14.56, 17.6) * mm, "end": v(14.56, 12.6) * mm});
            skLineSegment(sketch, "E50.right", {"start": v(19.56, 17.6) * mm, "end": v(19.56, 12.6) * mm});
            skSolve(sketch);
        }
        {
            var Q0;
            Q0=makeQuery(id+"F24.imprint","IMPRINT",FACE,{"disambiguationData":[TD([[makeQuery(id+"F24.imprint","IMPRINT",EDGE,{"derivedFrom":sQuery(id+"F24.wireOp",EDGE,"E50.bottom")}),-1.0]])]});
            extrude(context, id + "F25", {"entities" : qUnion([Q0]), "operationType" : NewBodyOperationType.ADD, "oppositeDirection" : true, "depth" : 10 * mm});
        }
        {
            var Q0;
            Q0=makeQuery(id+"F25.opExtrude","SWEPT_EDGE",EDGE,{"disambiguationData":[OSD([sQuery(id+"F24.wireOp",EDGE,"E50.bottom"),sQuery(id+"F24.wireOp",EDGE,"E50.right")])]});
            chamfer(context, id + "F26", {"entities" : qUnion([Q0]), "width" : 3 * mm, "tangentPropagation" : true});
        }
        {
            var Q0;
            Q0=qCreatedBy(makeId("Right.planeOp"),FACE);
            cPlane(context, id + "F27", {"entities" : qUnion([Q0]), "cplaneType" : CPlaneType.OFFSET, "offset" : 5 * mm, "width" : 150 * mm, "height" : 150 * mm});
        }
        {
            var Q0;
            Q0=makeQuery(id+"F1.opExtrude","SWEPT_BODY",BODY,{"disambiguationData":[OSD([sQuery(id+"F0.wireOp",EDGE,"E3.0"),sQuery(id+"F0.wireOp",EDGE,"E3.1"),sQuery(id+"F0.wireOp",EDGE,"E3.2"),sQuery(id+"F0.wireOp",EDGE,"E3.3"),sQuery(id+"F0.wireOp",EDGE,"E3.4"),sQuery(id+"F0.wireOp",EDGE,"E4"),sQuery(id+"F0.wireOp",EDGE,"E5.filletArc"),sQuery(id+"F0.wireOp",EDGE,"E6.filletArc")])]});
            var Q1;
            Q1=qCreatedBy(id+"F27.planeOp",FACE);
            mirror(context, id + "F28", {"entities" : qUnion([Q0]), "mirrorPlane" : qUnion([Q1])});
        }
        {
            var Q0;
            Q0=makeQuery(id+"F28.opPattern","COPY",FACE,{"derivedFrom":makeQuery(id+"F17.boolean.opBoolean","COPY",FACE,{"derivedFrom":makeQuery(id+"F17.opExtrude","CAP_FACE",FACE,{"disambiguationData":[OSD([sQuery(id+"F16.wireOp",EDGE,"E38.0"),sQuery(id+"F16.wireOp",EDGE,"E38.1"),sQuery(id+"F16.wireOp",EDGE,"E38.2"),sQuery(id+"F16.wireOp",EDGE,"E38.3"),sQuery(id+"F16.wireOp",EDGE,"E38.4"),sQuery(id+"F16.wireOp",EDGE,"E38.5")])],"isStart":false})}),"instanceName":"1"});
            var Q1;
            Q1=makeQuery(id+"F28.opPattern","COPY",FACE,{"derivedFrom":makeQuery(id+"F17.boolean.opBoolean","COPY",FACE,{"derivedFrom":makeQuery(id+"F17.opExtrude","CAP_FACE",FACE,{"disambiguationData":[OSD([sQuery(id+"F16.wireOp",EDGE,"E34.0"),sQuery(id+"F16.wireOp",EDGE,"E34.1"),sQuery(id+"F16.wireOp",EDGE,"E34.2"),sQuery(id+"F16.wireOp",EDGE,"E34.3"),sQuery(id+"F16.wireOp",EDGE,"E34.4"),sQuery(id+"F16.wireOp",EDGE,"E34.5")])],"isStart":false})}),"instanceName":"1"});
            var Q2;
            Q2=makeQuery(id+"F28.opPattern","COPY",FACE,{"derivedFrom":makeQuery(id+"F17.boolean.opBoolean","COPY",FACE,{"derivedFrom":makeQuery(id+"F17.opExtrude","CAP_FACE",FACE,{"disambiguationData":[OSD([sQuery(id+"F16.wireOp",EDGE,"E42.0"),sQuery(id+"F16.wireOp",EDGE,"E42.1"),sQuery(id+"F16.wireOp",EDGE,"E42.2"),sQuery(id+"F16.wireOp",EDGE,"E42.3"),sQuery(id+"F16.wireOp",EDGE,"E42.4"),sQuery(id+"F16.wireOp",EDGE,"E42.5")])],"isStart":false})}),"instanceName":"1"});
            extrude(context, id + "F29", {"entities" : qUnion([Q0, Q1, Q2]), "operationType" : NewBodyOperationType.ADD, "depth" : 6 * mm});
        }
        {
            var Q0;
            Q0=makeQuery(id+"F28.opPattern","COPY",FACE,{"derivedFrom":makeQuery(id+"F8.boolean.opBoolean","COPY",FACE,{"derivedFrom":makeQuery(id+"F8.opExtrude","CAP_FACE",FACE,{"disambiguationData":[OSD([sQuery(id+"F7.wireOp",EDGE,"E25.0"),sQuery(id+"F7.wireOp",EDGE,"E25.1"),sQuery(id+"F7.wireOp",EDGE,"E25.2"),sQuery(id+"F7.wireOp",EDGE,"E25.3"),sQuery(id+"F7.wireOp",EDGE,"E25.4"),sQuery(id+"F7.wireOp",EDGE,"E25.5")])],"isStart":false})}),"instanceName":"1"});
            extrude(context, id + "F30", {"entities" : qUnion([Q0]), "operationType" : NewBodyOperationType.ADD, "depth" : 10 * mm});
        }
        {
            var Q0;
            Q0=makeQuery(id+"F30.opExtrude","CAP_FACE",FACE,{"disambiguationData":[OSD([sQuery(id+"F7.wireOp",EDGE,"E25.0"),sQuery(id+"F7.wireOp",EDGE,"E25.1"),sQuery(id+"F7.wireOp",EDGE,"E25.2"),sQuery(id+"F7.wireOp",EDGE,"E25.3"),sQuery(id+"F7.wireOp",EDGE,"E25.4"),sQuery(id+"F7.wireOp",EDGE,"E25.5")])],"isStart":false});
            fillet(context, id + "F31", {"entities" : qUnion([Q0]), "radius" : .5 * mm, "tangentPropagation" : true, "allowEdgeOverflow" : false});
        }
    });
